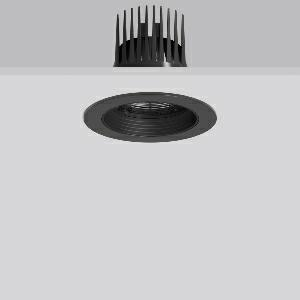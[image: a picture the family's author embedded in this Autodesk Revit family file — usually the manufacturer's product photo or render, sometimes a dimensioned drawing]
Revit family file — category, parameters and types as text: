
# Revit family: heledon_maxi_e_901768_003_3_012d
name_source: partatom
category: Lighting Fixtures
units: mm (PartAtom-declared; Revit-internal decimal feet)

## family parameters
Cut with Voids When Loaded = No
Host = Face
Light Source = No
Part Type = Normal
Room Calculation Point = No
Round Connector Dimension = Use Diameter
Shared = No

## types (1)
- HELEDON maxi E (1 x LED Modul 935, 3600 lm, 3500)
    Apparent Load = 35 VA
    Approval mark = CE
    CIE Flux Codes = 96 100 100 100 100
    Color Rendering = 92
    Color Temperature = 3500
    Default Elevation = 1800 mm
    Description = Series: HELEDON maxi
Round recessed downlight. Housing: die-cast aluminium, powder-coated. Black plastic ring and recessed LED to prevent glare from the side. Optical assembly with lens made of plastic (polycarbonate) for the best homogeneous light distribution - can be changed without tools. Best colour rendering index Ra>90. Suitable for Recessed ceiling mounting. Installation without tools thanks to spring fastening system. Including separate LED converter with connecting cable 600 mm.High quality converter without flickering and stroboscopic effect. Through-wiring box (5 pole) available as accessory. The following accessories can be mounted without use of tools: interchangeable lenses, decorative glasses, honeycomb louvre, clear and frosted diffusers, white interchangeable plastic ring. 
Colour: deep black, matt (RAL 9005)
Diameter: 162 mm
Height: 3 mm
Cut-out diameter: 152 mm
Recess height: 200 mm
Luminaire: recess height: 135 mm
Lamp: LED
Socket: without socket
Colour temperature: 3500K
Colour rendering index (CRI): 92
System power: 35 W
Rated luminous flux: 3600 lm
Luminous efficiency: 103 lm/W
Control gear: Regulated power supply
Protection class: II
Type of protection: IP 20
    Height = 0 mm  [stored 0 ft]
    Lamp = 1 x LED Modul 935
    Lamp Light Flux = 3600 lm
    Lamp count = 1
    Length = 162 mm
    Lifetime = 50000 h
    Luminous efficacy = 103 lm/W
    Manufacturer = RZB
    ModVariant = No
    Model = 901768.003.3
    Mounting Place = Ceiling
    Mounting Type = Recessed
    Number of Poles = 1
    OnlyDefault = Yes
    Power Factor = 1
    Product Name = HELEDON maxi E
    Product group = Recessed downlights
    ProductGroupID = 402
    Protection Class = Protection class II
    Protection Degree = IP 20
    RLX_Detail_Level = 1
    RLX_Emergency_Light_Flux = 0 lm
    RLX_Emergency_Type = 0
    RLX_Emergency_Type_DB = No
    RlxData = <blob elided: 121241 chars, md5=288beb51>
    Socket = socket
    Standby Power = 0 W
    System Light Flux = 3600 lm
    System Power = 35 W
    Type Comments = Product without accessories
    Type Image = 901663.003.jpg
    URL = http://relux.com
    VarID = ---
    Voltage = 230 V
    Voltage Range = 220-240 V
    Weight = 0.00 kg
    Width = 0 mm  [stored 0 ft]

note: [stored X ft] marks values corroborated as IEEE doubles in the binary element streams (Revit-internal decimal feet)

## geometry (parser evidence)
native form markers: Blend x4, Sweep x11
no freeform markers — native parametric forms only
